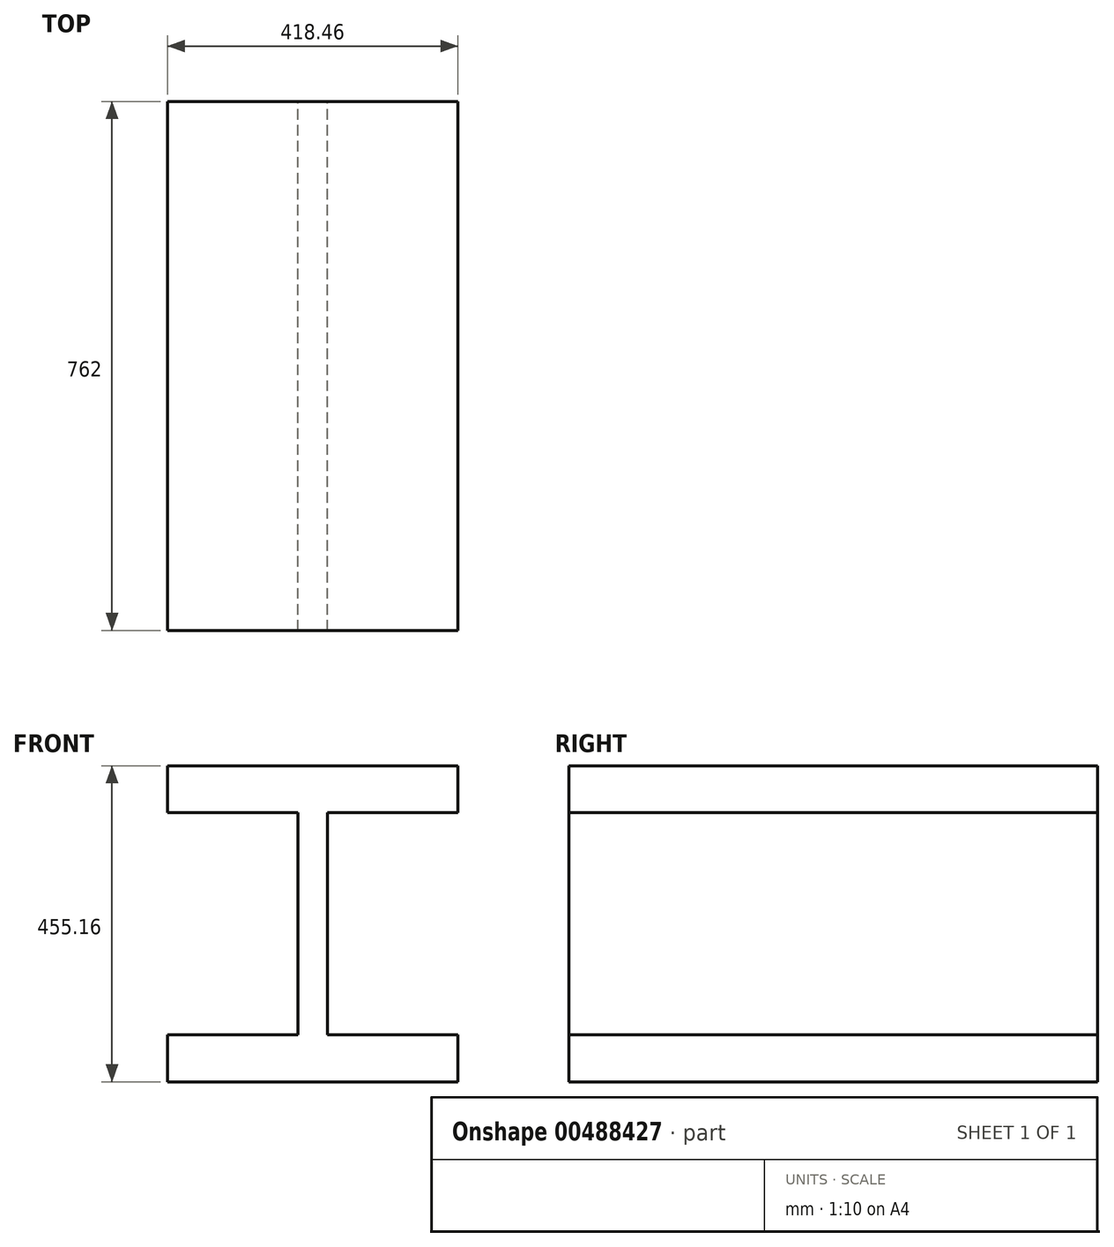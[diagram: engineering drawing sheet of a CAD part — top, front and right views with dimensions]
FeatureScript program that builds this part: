
annotation { "Feature Type Name" : "Feature", "Feature Type Description" : "" }
export const myFeature = defineFeature(function(context is Context, id is Id, definition is map)
    precondition{}
    {
        {
            var Q0;
            Q0=qCreatedBy(makeId("Front.planeOp"),FACE);
            var sketch = newSketch(context, id + "F0", { "sketchPlane" : qUnion([Q0])});
            skLineSegment(sketch, "E0", {"start": v(0, -428.52) * mm, "end": v(0, 307.08) * mm, "construction": true});
            skLineSegment(sketch, "E1", {"start": v(432.9, 0) * mm, "end": v(-493.72, 0) * mm, "construction": true});
            skLineSegment(sketch, "E2.bottom", {"start": v(-21.02, 160.02) * mm, "end": v(21.02, 160.02) * mm});
            skLineSegment(sketch, "E2.top", {"start": v(-21.02, -160.02) * mm, "end": v(21.02, -160.02) * mm});
            skLineSegment(sketch, "E2.left", {"start": v(-21.02, 160.02) * mm, "end": v(-21.02, -160.02) * mm});
            skLineSegment(sketch, "E2.right", {"start": v(21.02, 160.02) * mm, "end": v(21.02, -160.02) * mm});
            skPoint(sketch, "E2.middle", {"position": v(0, 0) * mm});
            skLineSegment(sketch, "E3.bottom", {"start": v(-209.23, 160.02) * mm, "end": v(209.23, 160.02) * mm});
            skLineSegment(sketch, "E3.top", {"start": v(-209.23, 227.58) * mm, "end": v(209.23, 227.58) * mm});
            skLineSegment(sketch, "E3.left", {"start": v(-209.23, 160.02) * mm, "end": v(-209.23, 227.58) * mm});
            skLineSegment(sketch, "E3.right", {"start": v(209.23, 160.02) * mm, "end": v(209.23, 227.58) * mm});
            skPoint(sketch, "E3.middle", {"position": v(0, 193.8) * mm});
            skLineSegment(sketch, "E4.bottom", {"start": v(-209.23, -160.02) * mm, "end": v(209.23, -160.02) * mm});
            skLineSegment(sketch, "E4.top", {"start": v(-209.23, -227.58) * mm, "end": v(209.23, -227.58) * mm});
            skLineSegment(sketch, "E4.left", {"start": v(-209.23, -160.02) * mm, "end": v(-209.23, -227.58) * mm});
            skLineSegment(sketch, "E4.right", {"start": v(209.23, -160.02) * mm, "end": v(209.23, -227.58) * mm});
            skPoint(sketch, "E4.middle", {"position": v(0, -193.8) * mm});
            skPoint(sketch, "E4.cornerSnap0", {"position": v(0, -160.02) * mm});
            skSolve(sketch);
        }
        {
            var Q0;
            Q0 = qSketchRegion(id + "F0", true);
            extrude(context, id + "F1", {"entities" : qUnion([Q0]), "depth" : 762 * mm, "offsetDistance" : 25.4 * mm});
        }
    });
